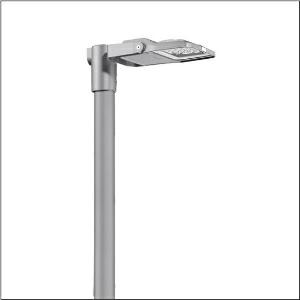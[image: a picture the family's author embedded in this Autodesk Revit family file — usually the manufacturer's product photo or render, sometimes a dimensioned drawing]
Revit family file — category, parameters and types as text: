
# Revit family: floodlight_fl_21_iq_micro___pl61_5xa7762a2c3a_d37b
name_source: partatom
category: Lighting Fixtures
units: mm (PartAtom-declared; Revit-internal decimal feet)

## family parameters
Cut with Voids When Loaded = No
Host = Face
Light Source = No
Part Type = Normal
Room Calculation Point = No
Round Connector Dimension = Use Diameter
Shared = No

## types (1)
- --- (1 x LED, 2910 lm, 23.1 W, 3000K)
    Apparent Load = 23 VA
    CIE Flux Codes = 33 65 98 100 100
    Color Rendering = 70
    Color Temperature = 3000K
    Default Elevation = 1800 mm
    Description = Floodlight FL 21 iQ micro, floodlight, primary light control with lens, of PMMA, primary optical cover: protective disc, of toughened safety glass, transparent, light distribution: PL61, light emission: direct distribution, installation type: surface-mounted, lamps: LED, High Power LED, rated values: 2.910lm | 23,1W | 126lm/W (begin service life); end service life: 2.910lm | 23,8W; at 50% lumin. flux: 1.455lm | 11W | 132,3lm/W, colour temperature: 3000K, colour rendering: CRI > 70, light colour: 730, light setting 1 begin service life: 100% | 2.910lm | 23,1W | 126lm/W | 3.000K, light setting 1 end service life: 23,8W, further light settings possible, control: Auto-Match, Temp-Guard, Night-Set, Smart-Wire, Desk-Remote (wireless, voltage-free reading and setting of iQ features in the workshop via application-optimized NFC function/RFID function), optimised constant luminous flux control (CLO 2.0), Street-Remote, pre-setting: linear dimming characteristic, with terminal, 6-pole, mains connection: 220..240V, AC, 50/60Hz, luminaire housing, of diecast aluminium, powder-coated, SITECO metallic grey (DB 702S), corrosivity category C5 mid according to DIN EN ISO 12944suitable for swimming poolschlorine-resistant, sealing non-destructively replaceable, please order mast flange separately, mast bracket, of steel, galvanised, powder-coated, SITECO metallic grey (DB 702S), protection rating (complete): IP66, insulation class (complete): insulation class II (safety insulation), certification: CE, ENEC, VDE, protection symbol: D, impact resistance: IK07, permissible operating ambient temperature: -40..+40°C, permissible operating ambient temperature for outdoor applications: -40..+50°C, standard: DIN EN 12944, LABS conformity tested according to VDMA 24364:2018-05, packaging unit: 1 piece

Light Distribution: PL61
    Height = 65 mm
    Lamp = 1 x LED
    Lamp Light Flux = 2910 lm
    Lamp Power = 23.1 W
    Lamp count = 1
    Length = 312 mm
    Luminous efficacy = 126 lm/W
    Manufacturer = Siteco
    ModVariant = No
    Model = 5XA7762A2C3A
    Mounting Place = Pole
    Mounting Type = Pole annexe
    Number of Poles = 1
    OnlyDefault = Yes
    Power Factor = 1
    Product Name = Floodlight FL 21 iQ micro | PL61
    Product group = floodlight | pylon annexe
    ProductGroupID = 6201
    Protection Class = Protection class II
    Protection Degree = IP 66
    RLX_Detail_Level = 1
    RLX_Emergency_Light_Flux = 0 lm
    RLX_Emergency_Type = 0
    RLX_Emergency_Type_DB = No
    RlxData = <blob elided: 102093 chars, md5=0ce99062>
    Socket = socket
    Standby Power = 0 W
    System Light Flux = 2910 lm
    System Power = 23 W
    Type Comments = factory setting: luminous flux: 100 % | dim-lin: 254 | 455 mA
    Type Image = l_1007121.jpg
    URL = http://relux.com
    VarID = @adj_193389
    Voltage = 0 V
    Weight = 0.00 kg
    Width = 230 mm

## geometry (parser evidence)
native form markers: Blend x4, Sweep x13
no freeform markers — native parametric forms only
